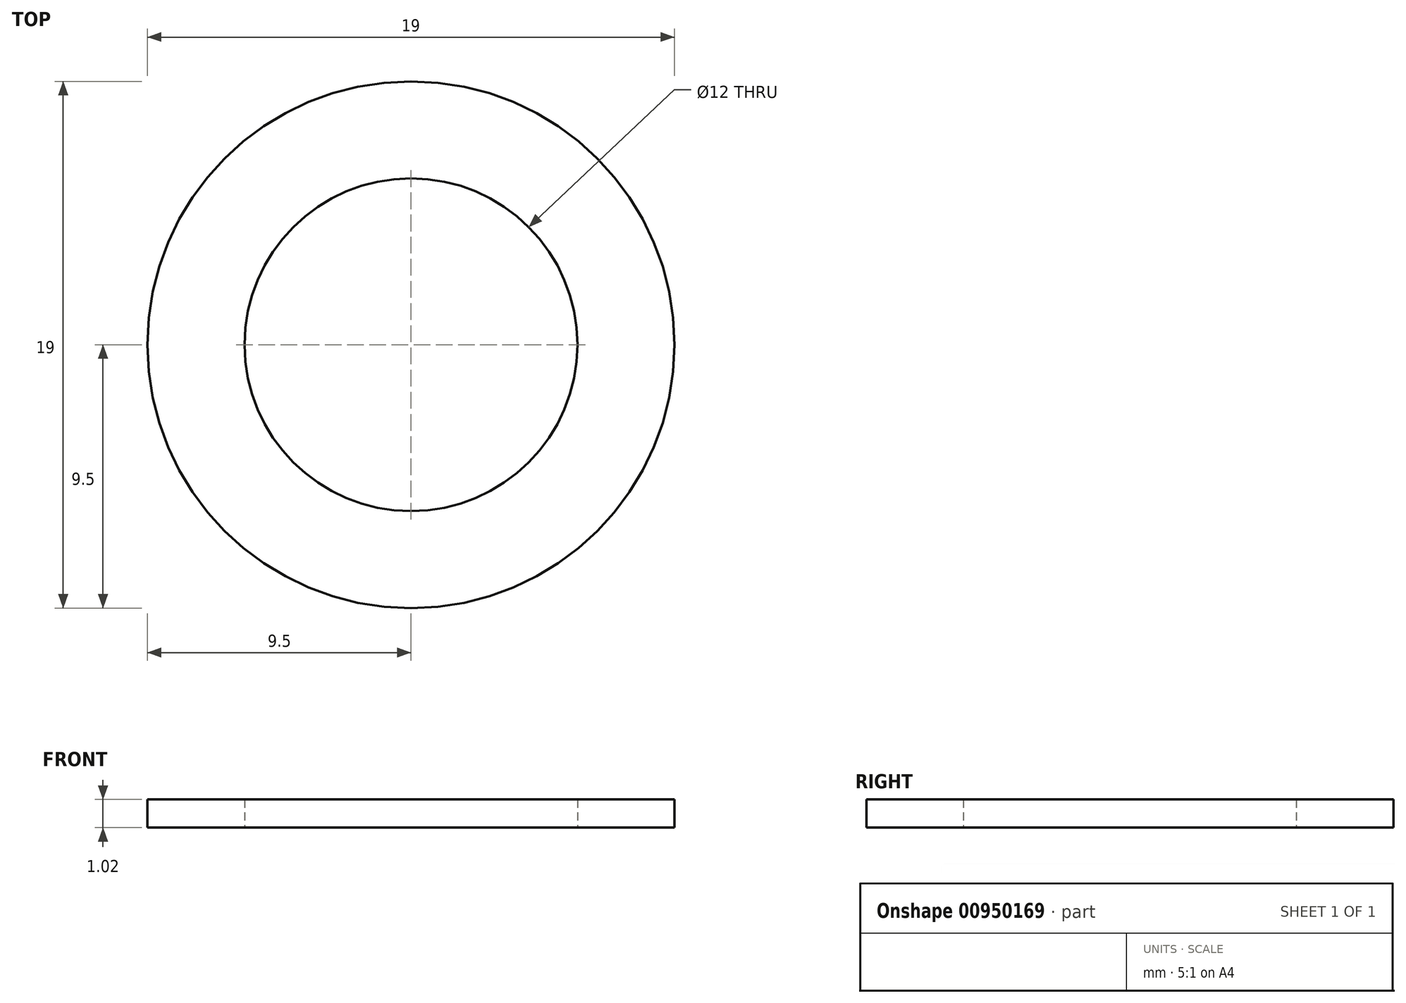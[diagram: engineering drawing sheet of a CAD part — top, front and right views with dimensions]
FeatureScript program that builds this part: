
annotation { "Feature Type Name" : "Feature", "Feature Type Description" : "" }
export const myFeature = defineFeature(function(context is Context, id is Id, definition is map)
    precondition{}
    {
        {
            var Q0;
            Q0=qCreatedBy(makeId("Top.planeOp"),FACE);
            var sketch = newSketch(context, id + "F0", { "sketchPlane" : qUnion([Q0])});
            skCircle(sketch, "E0", {"center": v(0, 0) * mm, "radius": 6 * mm});
            skCircle(sketch, "E1", {"center": v(0, 0) * mm, "radius": 9.5 * mm});
            skSolve(sketch);
        }
        {
            var Q0;
            Q0 = qSketchRegion(id + "F0", true);
            extrude(context, id + "F1", {"entities" : qUnion([Q0]), "depth" : 1.02 * mm, "offsetDistance" : 25.4 * mm});
        }
    });
